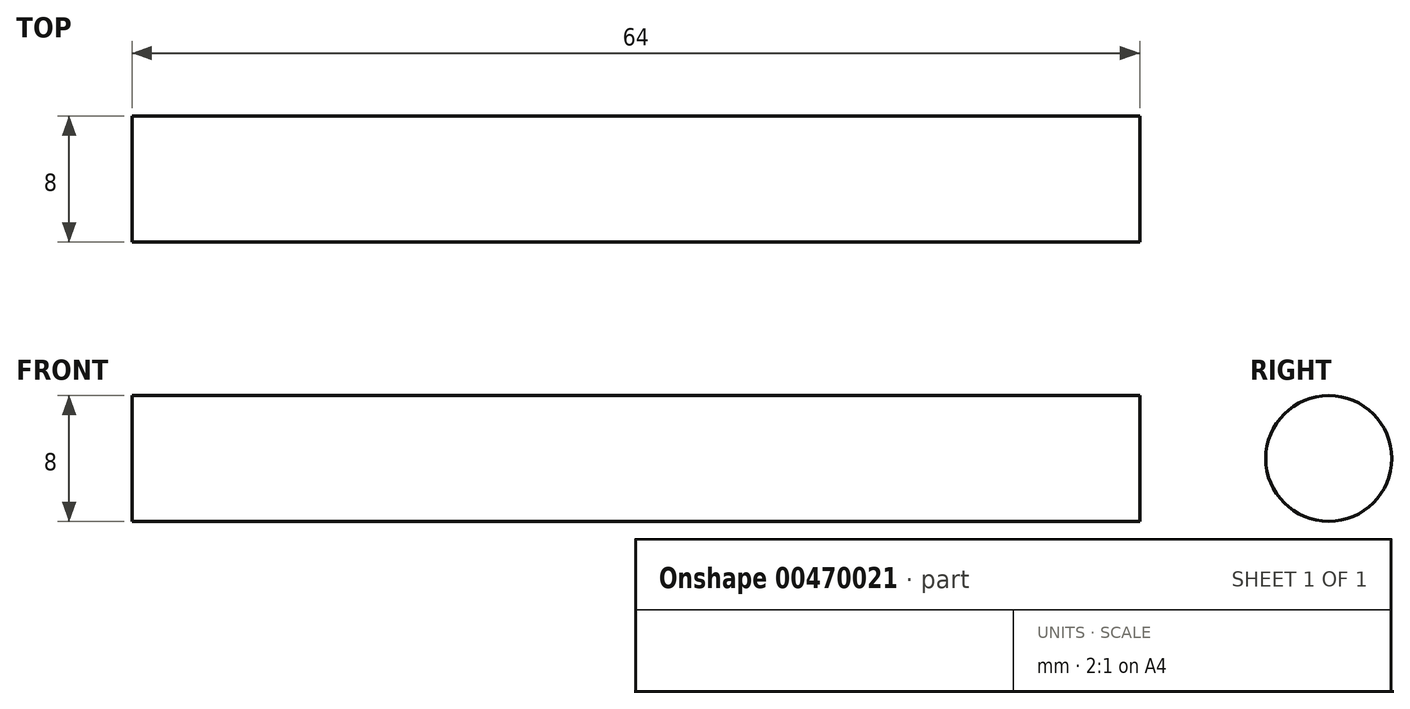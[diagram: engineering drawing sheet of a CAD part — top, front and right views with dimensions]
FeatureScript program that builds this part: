
annotation { "Feature Type Name" : "Feature", "Feature Type Description" : "" }
export const myFeature = defineFeature(function(context is Context, id is Id, definition is map)
    precondition{}
    {
        {
            var Q0;
            Q0=qCreatedBy(makeId("Right.planeOp"),FACE);
            var sketch = newSketch(context, id + "F0", { "sketchPlane" : qUnion([Q0])});
            skCircle(sketch, "E0", {"center": v(0, 0) * mm, "radius": 4 * mm});
            skSolve(sketch);
        }
        {
            var Q0;
            Q0=makeQuery(id+"F0.imprint","IMPRINT",FACE,{"disambiguationData":[TD([[makeQuery(id+"F0.imprint","IMPRINT",EDGE,{"derivedFrom":sQuery(id+"F0.wireOp",EDGE,"E0")}),1.0]])]});
            extrude(context, id + "F1", {"entities" : qUnion([Q0]), "depth" : 64 * mm, "offsetDistance" : 25 * mm});
        }
    });
